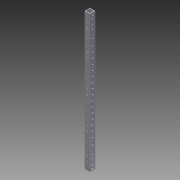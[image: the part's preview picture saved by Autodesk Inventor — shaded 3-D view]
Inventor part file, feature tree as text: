
AUTODESK INVENTOR PART (.ipt)
format: ipt  version: 2014 SP1 (Build 180222100, 222)  size: 203,264 bytes
history: native  units: in
note: dims shown in document units (in); Inventor stores cm internally (conversion verified against a paired STEP export)
features: extrude x4, sketch x4, reference x4
ambient origin geometry x8: Origin, YZ Plane, XZ Plane, XY Plane, X Axis, Y Axis, Z Axis, Center Point
bodies: Solid1 (feature_tree)
feature tree (12):
  extrude  "Extrusion1"  Depth=1.0in
  extrude  "Extrusion2"  Depth=26.0in TaperAngle=0.0deg
  extrude  "Extrusion3"  Depth=1.5in
  extrude  "Extrusion4"  Depth=1.0in
  sketch  "Sketch1"  dims[d0=1.0in d1=1.0in]
  sketch  "Sketch2"  dims[d2=0.125in d3=26.0in d4=0.0in]
  sketch  "Sketch3"  dims[d5=0.225in d6=1.5in]
  reference  "Reference5"
  reference  "Reference6"
  reference  "Reference7"
  reference  "Reference8"
  sketch  "Sketch4"  dims[d7=26.0in d8=9.4488in d10=1.0in d11=0.3937in d13=1.0in d15=1.0in d16=0.0in d17=0.26in d25=1.0in d26=0.0in d27=0.26in d28=0.26in d29=4.25in d30=4.25in d31=17.5in d32=1.25in d33=0.26in d34=6.2992in d36=1.0in d37=0.3937in d39=1.0in d41=1.0in d42=0.75in d43=0.26in d45=1.0in d46=0.75in d47=1.0in d48=0.0in]
